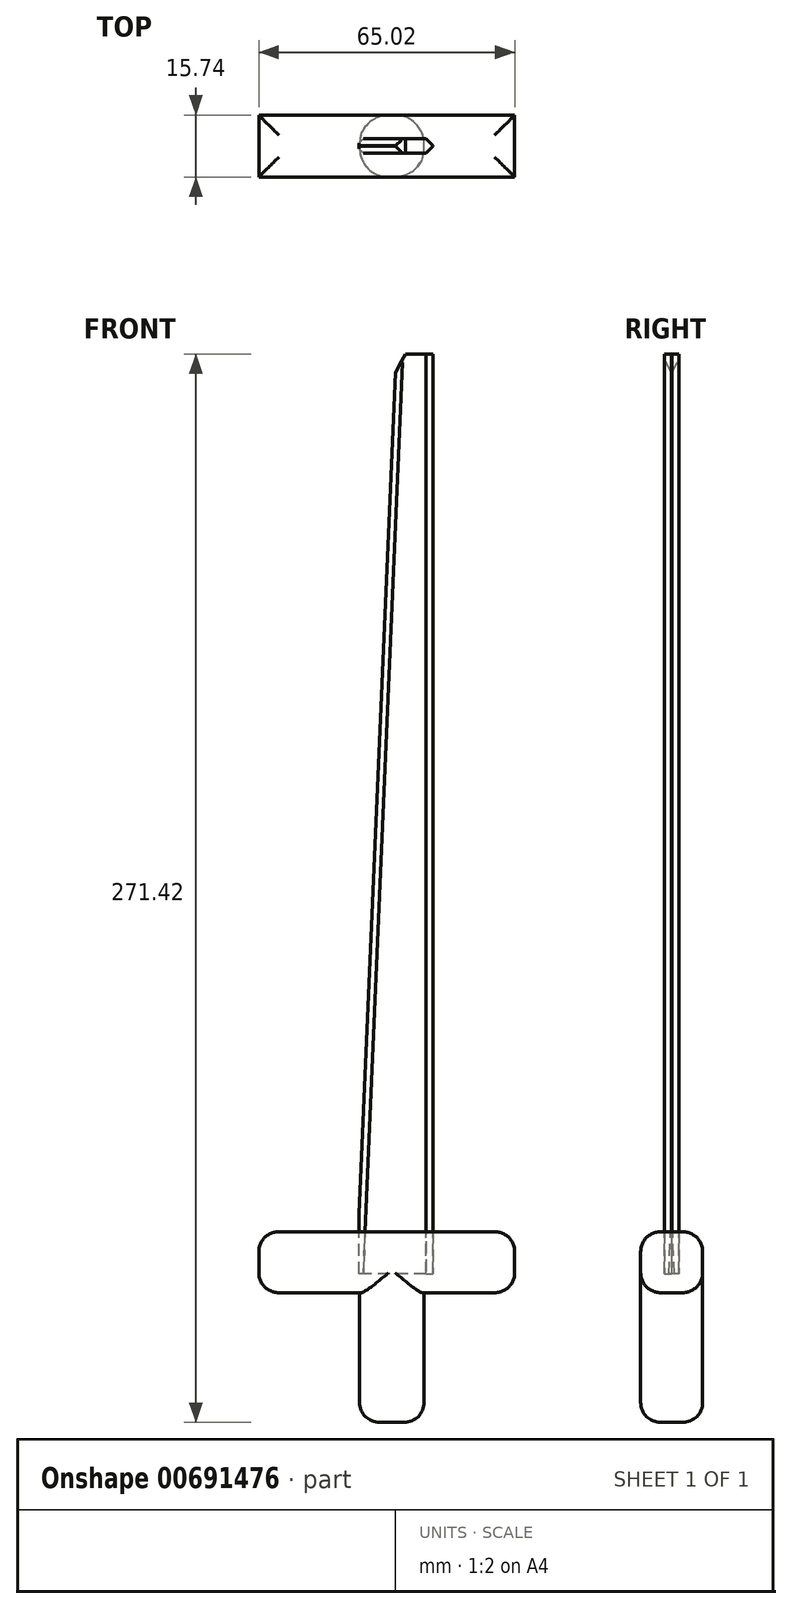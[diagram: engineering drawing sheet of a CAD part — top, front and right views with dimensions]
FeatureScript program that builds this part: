
annotation { "Feature Type Name" : "Feature", "Feature Type Description" : "" }
export const myFeature = defineFeature(function(context is Context, id is Id, definition is map)
    precondition{}
    {
        {
            var Q0;
            Q0=qCreatedBy(makeId("Front.planeOp"),FACE);
            var sketch = newSketch(context, id + "F0", { "sketchPlane" : qUnion([Q0])});
            skLineSegment(sketch, "E0.bottom", {"start": v(-34.86, 10.72) * mm, "end": v(30.16, 10.72) * mm});
            skLineSegment(sketch, "E0.top", {"start": v(-34.86, -4.8) * mm, "end": v(30.16, -4.8) * mm});
            skLineSegment(sketch, "E0.left", {"start": v(-34.86, 10.72) * mm, "end": v(-34.86, -4.8) * mm});
            skLineSegment(sketch, "E0.right", {"start": v(30.16, 10.72) * mm, "end": v(30.16, -4.8) * mm});
            skLineSegment(sketch, "E1.bottom", {"start": v(-9.24, 10.72) * mm, "end": v(7.15, 10.72) * mm});
            skLineSegment(sketch, "E1.top", {"start": v(-9.24, -37.74) * mm, "end": v(7.15, -37.74) * mm});
            skLineSegment(sketch, "E1.left", {"start": v(-9.24, 10.72) * mm, "end": v(-9.24, -37.74) * mm});
            skLineSegment(sketch, "E1.right", {"start": v(7.15, 10.72) * mm, "end": v(7.15, -37.74) * mm});
            skSolve(sketch);
        }
        {
            var Q0;
            Q0 = qSketchRegion(id + "F0", true);
            extrude(context, id + "F1", {"entities" : qUnion([Q0]), "endBound" : BoundingType.SYMMETRIC, "depth" : 15.75 * mm, "offsetDistance" : 25.4 * mm});
        }
        {
            var Q0;
            Q0=makeQuery(id+"F1.opExtrude","CAP_EDGE",EDGE,{"disambiguationData":[OSD([sQuery(id+"F0.wireOp",EDGE,"E1.left")])],"isStart":true});
            var Q1;
            Q1=makeQuery(id+"F1.opExtrude","CAP_EDGE",EDGE,{"disambiguationData":[OSD([sQuery(id+"F0.wireOp",EDGE,"E1.right")])],"isStart":true});
            var Q2;
            Q2=makeQuery(id+"F1.opExtrude","CAP_EDGE",EDGE,{"disambiguationData":[OSD([sQuery(id+"F0.wireOp",EDGE,"E1.left")])],"isStart":false});
            var Q3;
            Q3=makeQuery(id+"F1.opExtrude","CAP_EDGE",EDGE,{"disambiguationData":[OSD([sQuery(id+"F0.wireOp",EDGE,"E1.right")])],"isStart":false});
            fillet(context, id + "F2", {"entities" : qUnion([Q0, Q1, Q2, Q3]), "radius" : 7.36 * mm, "tangentPropagation" : true, "allowEdgeOverflow" : false});
        }
        {
            var Q0;
            Q0=makeQuery(id+"F1.opExtrude","SWEPT_EDGE",EDGE,{"disambiguationData":[OSD([sQuery(id+"F0.wireOp",EDGE,"E0.bottom"),sQuery(id+"F0.wireOp",EDGE,"E0.right")])]});
            var Q1;
            Q1=makeQuery(id+"F1.opExtrude","SWEPT_EDGE",EDGE,{"disambiguationData":[OSD([sQuery(id+"F0.wireOp",EDGE,"E0.bottom"),sQuery(id+"F0.wireOp",EDGE,"E0.left")])]});
            var Q2;
            Q2=makeQuery(id+"F1.opExtrude","SWEPT_EDGE",EDGE,{"disambiguationData":[OSD([sQuery(id+"F0.wireOp",EDGE,"E0.top"),sQuery(id+"F0.wireOp",EDGE,"E0.left")])]});
            var Q3;
            Q3=makeQuery(id+"F1.opExtrude","SWEPT_EDGE",EDGE,{"disambiguationData":[OSD([sQuery(id+"F0.wireOp",EDGE,"E0.top"),sQuery(id+"F0.wireOp",EDGE,"E0.right")])]});
            var Q4;
            {var subQ0=sQuery(id+"F0.wireOp",EDGE,"E0.top");Q4=makeQuery(id+"F1.opExtrude","CAP_EDGE",EDGE,{"disambiguationData":[OSD([subQ0]),TDD([makeQuery(id+"F0.imprint","IMPRINT",EDGE,{"disambiguationData":[TD([[makeQuery(id+"F0.imprint","INTERSECT",VERTEX,{"derivedFrom":[subQ0,sQuery(id+"F0.wireOp",EDGE,"E0.right")]}),1.0]])],"derivedFrom":subQ0})])],"isStart":false});}
            var Q5;
            {var subQ0=sQuery(id+"F0.wireOp",EDGE,"E0.top");Q5=makeQuery(id+"F1.opExtrude","CAP_EDGE",EDGE,{"disambiguationData":[OSD([subQ0]),TDD([makeQuery(id+"F0.imprint","IMPRINT",EDGE,{"disambiguationData":[TD([[makeQuery(id+"F0.imprint","INTERSECT",VERTEX,{"derivedFrom":[subQ0,sQuery(id+"F0.wireOp",EDGE,"E0.left")]}),-1.0]])],"derivedFrom":subQ0})])],"isStart":false});}
            var Q6;
            Q6=makeQuery(id+"F1.opExtrude","CAP_EDGE",EDGE,{"disambiguationData":[OSD([sQuery(id+"F0.wireOp",EDGE,"E0.bottom"),sQuery(id+"F0.wireOp",EDGE,"E1.bottom")])],"isStart":false});
            var Q7;
            Q7=makeQuery(id+"F1.opExtrude","CAP_EDGE",EDGE,{"disambiguationData":[OSD([sQuery(id+"F0.wireOp",EDGE,"E0.bottom"),sQuery(id+"F0.wireOp",EDGE,"E1.bottom")])],"isStart":true});
            var Q8;
            {var subQ0=sQuery(id+"F0.wireOp",EDGE,"E0.top");Q8=makeQuery(id+"F1.opExtrude","CAP_EDGE",EDGE,{"disambiguationData":[OSD([subQ0]),TDD([makeQuery(id+"F0.imprint","IMPRINT",EDGE,{"disambiguationData":[TD([[makeQuery(id+"F0.imprint","INTERSECT",VERTEX,{"derivedFrom":[subQ0,sQuery(id+"F0.wireOp",EDGE,"E0.right")]}),1.0]])],"derivedFrom":subQ0})])],"isStart":true});}
            var Q9;
            {var subQ0=sQuery(id+"F0.wireOp",EDGE,"E0.top");Q9=makeQuery(id+"F1.opExtrude","CAP_EDGE",EDGE,{"disambiguationData":[OSD([subQ0]),TDD([makeQuery(id+"F0.imprint","IMPRINT",EDGE,{"disambiguationData":[TD([[makeQuery(id+"F0.imprint","INTERSECT",VERTEX,{"derivedFrom":[subQ0,sQuery(id+"F0.wireOp",EDGE,"E0.left")]}),-1.0]])],"derivedFrom":subQ0})])],"isStart":true});}
            fillet(context, id + "F3", {"entities" : qUnion([Q0, Q1, Q2, Q3, Q4, Q5, Q6, Q7, Q8, Q9]), "radius" : 5.08 * mm, "tangentPropagation" : true, "allowEdgeOverflow" : false});
        }
        {
            var Q0;
            Q0=makeQuery(id+"F2.opFillet","BLEND_EDGE",EDGE,{"blendedFrom":[makeQuery(id+"F1.opExtrude","CAP_EDGE",EDGE,{"disambiguationData":[OSD([sQuery(id+"F0.wireOp",EDGE,"E1.right")])],"isStart":true}),makeQuery(id+"F1.opExtrude","SWEPT_FACE",FACE,{"disambiguationData":[OSD([sQuery(id+"F0.wireOp",EDGE,"E1.top")])]})],"blendedInto":[makeQuery(id+"F1.opExtrude","SWEPT_FACE",FACE,{"disambiguationData":[OSD([sQuery(id+"F0.wireOp",EDGE,"E1.top")])]})]});
            fillet(context, id + "F4", {"entities" : qUnion([Q0]), "radius" : 5.08 * mm, "tangentPropagation" : true, "allowEdgeOverflow" : false});
        }
        {
            var Q0;
            Q0=qCreatedBy(makeId("Top.planeOp"),FACE);
            var sketch = newSketch(context, id + "F5", { "sketchPlane" : qUnion([Q0])});
            skLineSegment(sketch, "E2.bottom", {"start": v(9.41, 1.83) * mm, "end": v(-9.41, 1.83) * mm});
            skLineSegment(sketch, "E2.top", {"start": v(9.41, -1.83) * mm, "end": v(-9.41, -1.83) * mm});
            skLineSegment(sketch, "E2.left", {"start": v(9.41, 1.83) * mm, "end": v(9.41, -1.83) * mm});
            skLineSegment(sketch, "E2.right", {"start": v(-9.41, 1.83) * mm, "end": v(-9.41, -1.83) * mm});
            skPoint(sketch, "E2.middle", {"position": v(0, 0) * mm});
            skSolve(sketch);
        }
        {
            var Q0;
            Q0 = qSketchRegion(id + "F5", true);
            extrude(context, id + "F6", {"entities" : qUnion([Q0]), "depth" : 233.68 * mm, "offsetDistance" : 25.4 * mm});
        }
        {
            var Q0;
            Q0=qCreatedBy(makeId("Front.planeOp"),FACE);
            var sketch = newSketch(context, id + "F7", { "sketchPlane" : qUnion([Q0])});
            skLineSegment(sketch, "E3", {"start": v(0, 233.45) * mm, "end": v(-9.57, 11.57) * mm});
            skLineSegment(sketch, "E4", {"start": v(-9.57, 11.57) * mm, "end": v(-87.93, 41.84) * mm});
            skLineSegment(sketch, "E5", {"start": v(-87.93, 40.86) * mm, "end": v(-14.18, 233.45) * mm});
            skLineSegment(sketch, "E6", {"start": v(-14.18, 233.45) * mm, "end": v(-6.03, 240.19) * mm});
            skLineSegment(sketch, "E7", {"start": v(-6.03, 240.19) * mm, "end": v(0, 233.45) * mm});
            skSolve(sketch);
        }
        {
            var Q0;
            Q0 = qSketchRegion(id + "F7", true);
            extrude(context, id + "F8", {"entities" : qUnion([Q0]), "operationType" : NewBodyOperationType.REMOVE, "endBound" : BoundingType.SYMMETRIC, "depth" : 135.13 * mm, "offsetDistance" : 25.4 * mm});
        }
        {
            var Q0;
            Q0=makeQuery(id+"F8.boolean.opBoolean","INTERSECT",EDGE,{"derivedFrom":[makeQuery(id+"F6.opExtrude","SWEPT_FACE",FACE,{"disambiguationData":[OSD([sQuery(id+"F5.wireOp",EDGE,"E2.bottom")])]}),makeQuery(id+"F8.opExtrude","SWEPT_FACE",FACE,{"disambiguationData":[OSD([sQuery(id+"F7.wireOp",EDGE,"E3")])]})]});
            var Q1;
            Q1=makeQuery(id+"F8.boolean.opBoolean","INTERSECT",EDGE,{"derivedFrom":[makeQuery(id+"F6.opExtrude","SWEPT_FACE",FACE,{"disambiguationData":[OSD([sQuery(id+"F5.wireOp",EDGE,"E2.top")])]}),makeQuery(id+"F8.opExtrude","SWEPT_FACE",FACE,{"disambiguationData":[OSD([sQuery(id+"F7.wireOp",EDGE,"E3")])]})]});
            var Q2;
            Q2=makeQuery(id+"F6.opExtrude","SWEPT_EDGE",EDGE,{"disambiguationData":[OSD([sQuery(id+"F5.wireOp",EDGE,"E2.bottom"),sQuery(id+"F5.wireOp",EDGE,"E2.left")])]});
            var Q3;
            Q3=makeQuery(id+"F6.opExtrude","SWEPT_EDGE",EDGE,{"disambiguationData":[OSD([sQuery(id+"F5.wireOp",EDGE,"E2.top"),sQuery(id+"F5.wireOp",EDGE,"E2.left")])]});
            chamfer(context, id + "F9", {"entities" : qUnion([Q0, Q1, Q2, Q3]), "width" : 1.78 * mm, "tangentPropagation" : true});
        }
        {
            var Q0;
            Q0=qCreatedBy(makeId("Front.planeOp"),FACE);
            var sketch = newSketch(context, id + "F10", { "sketchPlane" : qUnion([Q0])});
            skLineSegment(sketch, "E8", {"start": v(-0.3, 228.85) * mm, "end": v(2.68, 234.23) * mm});
            skLineSegment(sketch, "E9", {"start": v(2.68, 234.23) * mm, "end": v(-2.7, 234.23) * mm});
            skLineSegment(sketch, "E10", {"start": v(-2.33, 234.23) * mm, "end": v(-2.7, 233.01) * mm});
            skLineSegment(sketch, "E11", {"start": v(-2.7, 233.01) * mm, "end": v(-0.3, 228.85) * mm});
            skSolve(sketch);
        }
        {
            var Q0;
            Q0 = qSketchRegion(id + "F10", true);
            extrude(context, id + "F11", {"entities" : qUnion([Q0]), "operationType" : NewBodyOperationType.REMOVE, "endBound" : BoundingType.SYMMETRIC, "oppositeDirection" : true, "depth" : 29.97 * mm, "offsetDistance" : 25.4 * mm});
        }
    });
